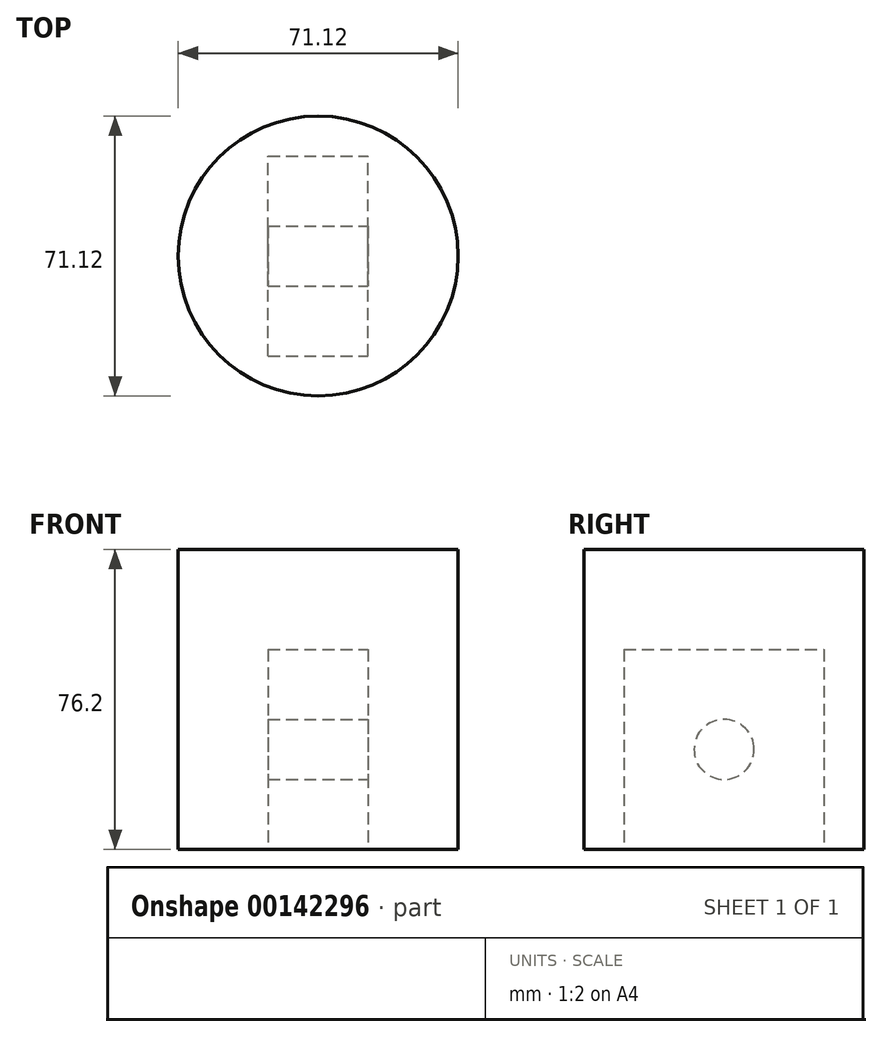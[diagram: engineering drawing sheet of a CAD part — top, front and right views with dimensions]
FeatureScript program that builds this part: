
annotation { "Feature Type Name" : "Feature", "Feature Type Description" : "" }
export const myFeature = defineFeature(function(context is Context, id is Id, definition is map)
    precondition{}
    {
        {
            var Q0;
            Q0=qCreatedBy(makeId("Top.planeOp"),FACE);
            var sketch = newSketch(context, id + "F0", { "sketchPlane" : qUnion([Q0])});
            skCircle(sketch, "E0", {"center": v(0, 0) * mm, "radius": 35.56 * mm});
            skSolve(sketch);
        }
        {
            var Q0;
            Q0 = qSketchRegion(id + "F0", true);
            extrude(context, id + "F1", {"entities" : qUnion([Q0]), "depth" : 76.2 * mm});
        }
        {
            var Q0;
            Q0=makeQuery(id+"F1.opExtrude","CAP_FACE",FACE,{"disambiguationData":[OSD([sQuery(id+"F0.wireOp",EDGE,"E0")])],"isStart":true});
            var sketch = newSketch(context, id + "F2", { "sketchPlane" : qUnion([Q0])});
            skLineSegment(sketch, "E1.bottom", {"start": v(-12.7, 25.4) * mm, "end": v(12.7, 25.4) * mm});
            skLineSegment(sketch, "E1.top", {"start": v(-12.7, -25.4) * mm, "end": v(12.7, -25.4) * mm});
            skLineSegment(sketch, "E1.left", {"start": v(-12.7, 25.4) * mm, "end": v(-12.7, -25.4) * mm});
            skLineSegment(sketch, "E1.right", {"start": v(12.7, 25.4) * mm, "end": v(12.7, -25.4) * mm});
            skSolve(sketch);
        }
        {
            var Q0;
            Q0 = qSketchRegion(id + "F2", true);
            extrude(context, id + "F3", {"entities" : qUnion([Q0]), "operationType" : NewBodyOperationType.REMOVE, "oppositeDirection" : true, "depth" : 50.8 * mm});
        }
        {
            var Q0;
            Q0=qCreatedBy(makeId("Right.planeOp"),FACE);
            cPlane(context, id + "F4", {"entities" : qUnion([Q0]), "cplaneType" : CPlaneType.OFFSET, "offset" : 33.02 * mm, "width" : 152.4 * mm, "height" : 152.4 * mm});
        }
        {
            var Q0;
            Q0=qCreatedBy(id+"F4.planeOp",FACE);
            var sketch = newSketch(context, id + "F5", { "sketchPlane" : qUnion([Q0])});
            skCircle(sketch, "E2", {"center": v(0, 25.4) * mm, "radius": 7.62 * mm});
            skSolve(sketch);
        }
        {
            var Q0;
            Q0 = qSketchRegion(id + "F5", true);
            var Q1;
            Q1=makeQuery(id+"F1.opExtrude","SWEPT_FACE",FACE,{"disambiguationData":[OSD([sQuery(id+"F0.wireOp",EDGE,"E0")])]});
            extrude(context, id + "F6", {"entities" : qUnion([Q0]), "operationType" : NewBodyOperationType.ADD, "oppositeDirection" : true, "endBoundEntityFace" : qUnion([Q1]), "depth" : 66.04 * mm});
        }
    });
